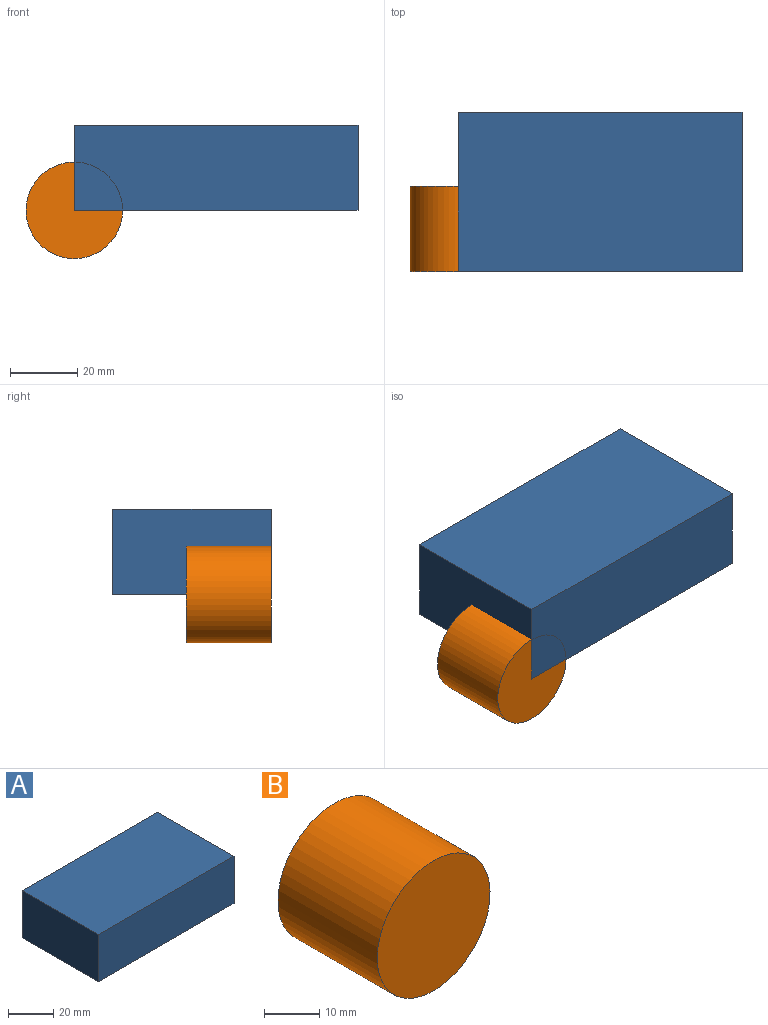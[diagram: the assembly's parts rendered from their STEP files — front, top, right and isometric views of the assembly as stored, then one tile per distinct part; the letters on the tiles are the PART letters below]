
ASSEMBLY  parts=2 mates=1
PART A: 6 faces, bbox 84.6x47.4x25.4 mm
  f0: plane 84.62x25.4mm, normal (0,1,0), area 2149.2mm2, adj f1,f3,f4,f5
  f1: plane 47.41x25.4mm, normal (-1,0,0), area 1204.1mm2, adj f0,f2,f4,f5
  f2: plane 84.62x25.4mm, normal (0,-1,0), area 2149.2mm2, adj f1,f3,f4,f5
  f3: plane 47.41x25.4mm, normal (1,0,0), area 1204.1mm2, adj f0,f2,f4,f5
  f4: plane 84.62x47.41mm, normal (0,0,1), area 4011.3mm2, adj f0,f1,f2,f3
  f5: plane 84.62x47.41mm, normal (0,0,-1), area 4011.3mm2, adj f0,f1,f2,f3
PART B: 3 faces, bbox 28.8x25.4x28.8 mm
  f0: cylinder r=14.41mm len=28.83mm, axis (0,1,0), area 2300.5mm2, adj f1,f2
  f1: plane 28.83x28.83mm, normal (0,-1,0), area 652.8mm2, adj f0
  f2: plane 28.83x28.83mm, normal (0,1,0), area 652.8mm2, adj f0
PLACE A at identity
PLACE B t=(-42.25,11.38,-3.37)mm
MATE revolute B.f0 <-> A.f2  axis (0,-1,0) through (-48.26,-14.02,0)mm
